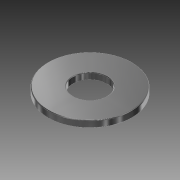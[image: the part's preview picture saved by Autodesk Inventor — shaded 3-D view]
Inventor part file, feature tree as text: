
AUTODESK INVENTOR PART (.ipt)
format: ipt  version: 2013 (Build 170138000, 138)  size: 108,032 bytes
history: native  units: mm
features: other x1, extrude x1, fillet x1, sketch x1
ambient origin geometry x1: Origin
feature tree (4):
  other  "ソリッド1"
  extrude  "押し出し1"  Depth=10.0mm
  fillet  "フィレット1"  Radius=4.0mm
  sketch  "スケッチ1"
